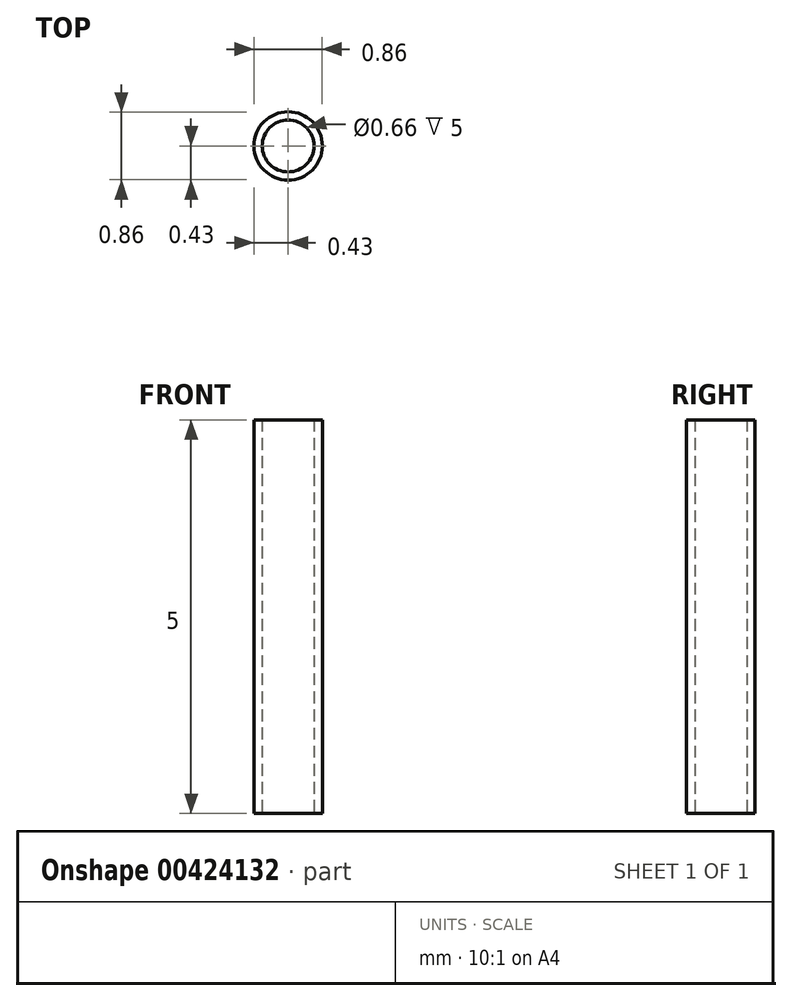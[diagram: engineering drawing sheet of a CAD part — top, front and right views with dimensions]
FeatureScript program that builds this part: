
annotation { "Feature Type Name" : "Feature", "Feature Type Description" : "" }
export const myFeature = defineFeature(function(context is Context, id is Id, definition is map)
    precondition{}
    {
        {
            var Q0;
            Q0=qCreatedBy(makeId("Top.planeOp"),FACE);
            var sketch = newSketch(context, id + "F0", { "sketchPlane" : qUnion([Q0])});
            skCircle(sketch, "E0", {"center": v(0, 0) * mm, "radius": 0.43 * mm});
            skCircle(sketch, "E1", {"center": v(0, 0) * mm, "radius": 0.33 * mm});
            skSolve(sketch);
        }
        {
            var Q0;
            Q0 = qSketchRegion(id + "F0", true);
            extrude(context, id + "F1", {"entities" : qUnion([Q0]), "depth" : 5 * mm});
        }
    });
